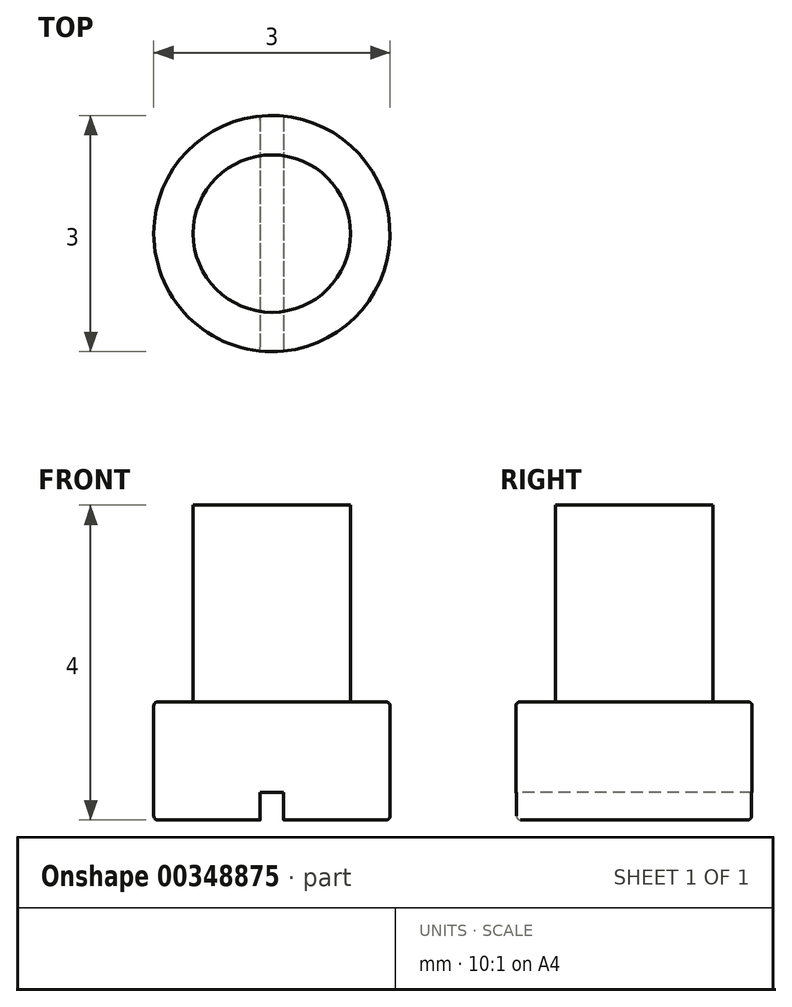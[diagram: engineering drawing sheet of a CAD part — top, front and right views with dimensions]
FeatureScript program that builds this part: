
annotation { "Feature Type Name" : "Feature", "Feature Type Description" : "" }
export const myFeature = defineFeature(function(context is Context, id is Id, definition is map)
    precondition{}
    {
        {
            var Q0;
            Q0=qCreatedBy(makeId("Front.planeOp"),FACE);
            var sketch = newSketch(context, id + "F0", { "sketchPlane" : qUnion([Q0])});
            skLineSegment(sketch, "E0", {"start": v(0, 0) * mm, "end": v(1.5, 0) * mm});
            skLineSegment(sketch, "E1", {"start": v(1.5, 0) * mm, "end": v(1.5, 1.5) * mm});
            skLineSegment(sketch, "E2", {"start": v(1.5, 1.5) * mm, "end": v(1, 1.5) * mm});
            skLineSegment(sketch, "E3", {"start": v(1, 1.5) * mm, "end": v(1, 4) * mm});
            skLineSegment(sketch, "E4", {"start": v(1, 4) * mm, "end": v(0, 4) * mm});
            skLineSegment(sketch, "E5", {"start": v(0, 4) * mm, "end": v(0, 0) * mm});
            skSolve(sketch);
        }
        {
            var Q0;
            Q0=qSketchRegion(id+"F0",true);
            var Q1;
            Q1=sQuery(id+"F0.wireOp",EDGE,"E5");
            revolve(context, id + "F1", {"entities" : qUnion([Q0]), "axis" : qUnion([Q1]), "revolveType" : RevolveType.FULL});
        }
        {
            var Q0;
            Q0=qCreatedBy(makeId("Front.planeOp"),FACE);
            var sketch = newSketch(context, id + "F2", { "sketchPlane" : qUnion([Q0])});
            skLineSegment(sketch, "E6", {"start": v(0, 0) * mm, "end": v(0, 1.97) * mm, "construction": true});
            skLineSegment(sketch, "E7.bottom", {"start": v(-0.15, 0) * mm, "end": v(0.15, 0) * mm});
            skLineSegment(sketch, "E7.top", {"start": v(-0.15, 0.35) * mm, "end": v(0.15, 0.35) * mm});
            skLineSegment(sketch, "E7.left", {"start": v(-0.15, 0) * mm, "end": v(-0.15, 0.35) * mm});
            skLineSegment(sketch, "E7.right", {"start": v(0.15, 0) * mm, "end": v(0.15, 0.35) * mm});
            skSolve(sketch);
        }
        {
            var Q0;
            Q0=qSketchRegion(id+"F2",true);
            extrude(context, id + "F3", {"entities" : qUnion([Q0]), "operationType" : NewBodyOperationType.REMOVE, "endBound" : BoundingType.SYMMETRIC, "oppositeDirection" : true, "depth" : 25 * mm});
        }
        {
            var Q0;
            Q0=makeQuery(id+"F1.opRevolve","SWEPT_EDGE",EDGE,{"disambiguationData":[OSD([sQuery(id+"F0.wireOp",EDGE,"E1"),sQuery(id+"F0.wireOp",EDGE,"E2")])]});
            var Q1;
            {var subQ0=sQuery(id+"F0.wireOp",EDGE,"E0");var subQ1=sQuery(id+"F0.wireOp",EDGE,"E1");Q1=makeQuery(id+"F3.boolean.opBoolean","SPLIT",EDGE,{"disambiguationData":[TD([makeQuery(id+"F3.opExtrude","SWEPT_FACE",FACE,{"disambiguationData":[OSD([sQuery(id+"F2.wireOp",EDGE,"E7.right")])]})])],"derivedFrom":makeQuery(id+"F1.opRevolve","SWEPT_EDGE",EDGE,{"disambiguationData":[OSD([subQ0,subQ1])]})});}
            var Q2;
            {var subQ0=sQuery(id+"F0.wireOp",EDGE,"E0");var subQ1=sQuery(id+"F0.wireOp",EDGE,"E1");Q2=makeQuery(id+"F3.boolean.opBoolean","SPLIT",EDGE,{"disambiguationData":[TD([makeQuery(id+"F3.opExtrude","SWEPT_FACE",FACE,{"disambiguationData":[OSD([sQuery(id+"F2.wireOp",EDGE,"E7.left")])]})])],"derivedFrom":makeQuery(id+"F1.opRevolve","SWEPT_EDGE",EDGE,{"disambiguationData":[OSD([subQ0,subQ1])]})});}
            fillet(context, id + "F4", {"entities" : qUnion([Q0, Q1, Q2]), "radius" : 0.05 * mm, "tangentPropagation" : true, "allowEdgeOverflow" : false});
        }
    });
